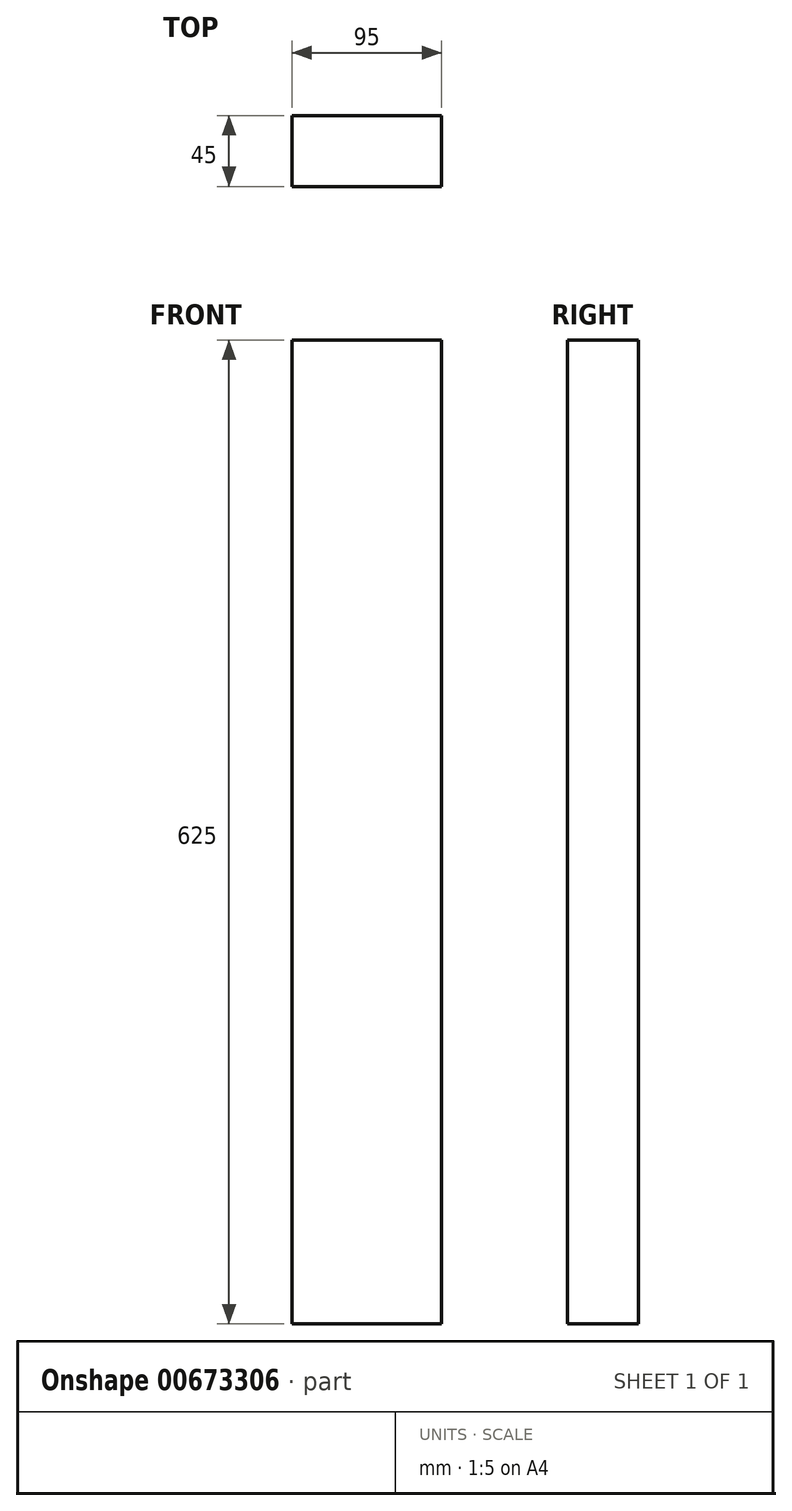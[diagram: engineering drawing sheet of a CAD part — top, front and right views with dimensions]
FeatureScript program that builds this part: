
annotation { "Feature Type Name" : "Feature", "Feature Type Description" : "" }
export const myFeature = defineFeature(function(context is Context, id is Id, definition is map)
    precondition{}
    {
        {
            var Q0;
            Q0=qCreatedBy(makeId("Top.planeOp"),FACE);
            var sketch = newSketch(context, id + "F0", { "sketchPlane" : qUnion([Q0])});
            skLineSegment(sketch, "E0.bottom", {"start": v(0, 0) * mm, "end": v(95, 0) * mm});
            skLineSegment(sketch, "E0.top", {"start": v(0, 45) * mm, "end": v(95, 45) * mm});
            skLineSegment(sketch, "E0.left", {"start": v(0, 0) * mm, "end": v(0, 45) * mm});
            skLineSegment(sketch, "E0.right", {"start": v(95, 0) * mm, "end": v(95, 45) * mm});
            skSolve(sketch);
        }
        {
            var Q0;
            Q0=qSketchRegion(id+"F0",true);
            extrude(context, id + "F1", {"entities" : qUnion([Q0]), "depth" : (750 - 125) * mm, "offsetDistance" : 25 * mm});
        }
    });
